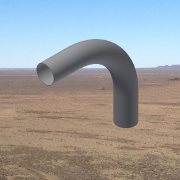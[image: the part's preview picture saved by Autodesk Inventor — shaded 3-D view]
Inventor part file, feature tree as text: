
AUTODESK INVENTOR PART (.ipt)
format: ipt  version: 2014 SP1 (Build 180222100, 222)  size: 180,224 bytes
history: native  units: in
note: dims shown in document units (in); Inventor stores cm internally (conversion verified against a paired STEP export)
features: sketch x4, extrude x2, plane x1, sweep x1
ambient origin geometry x8: Origin, YZ Plane, XZ Plane, XY Plane, X Axis, Y Axis, Z Axis, Center Point
bodies: Solid1 (feature_tree)
feature tree (8):
  extrude  "Extrusion1"  Depth=0.1in
  sketch  "Sketch4"  dims[d2=6.0in d3=0.0in d7=12.0in]
  plane  "Work Plane4"
  sweep  "Sweep1"
  extrude  "Extrusion2"  Depth=6.0in TaperAngle=0.0deg
  sketch  "Sketch1"  dims[d0=3.937in d1=0.1in]
  sketch  "Sketch8"  dims[d9=0.0in d10=6.0in d11=0.0in]
  sketch  "Sketch9"
